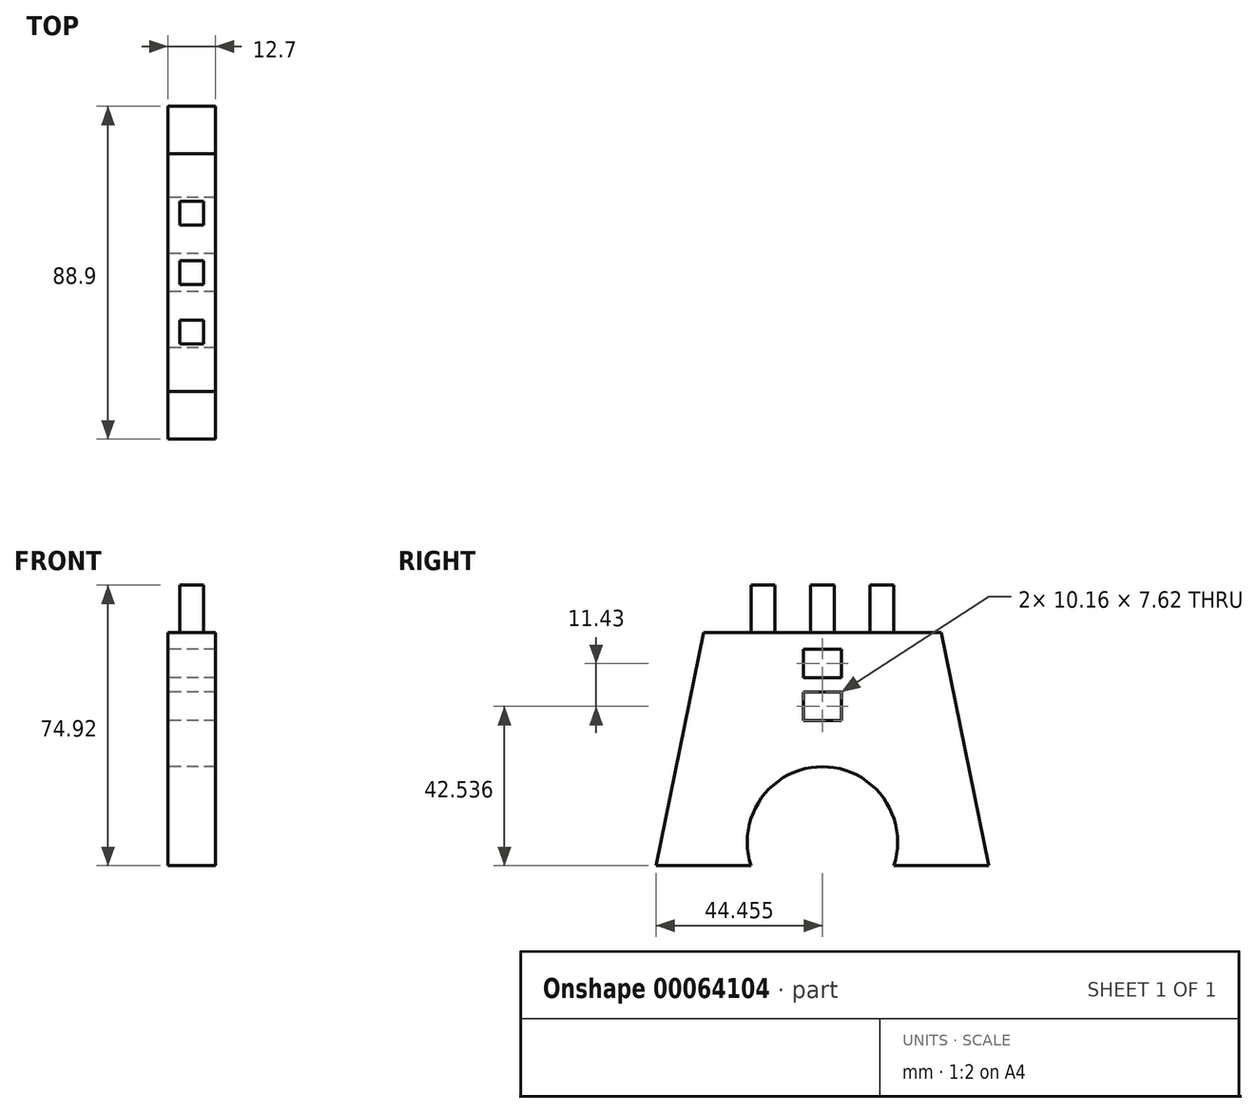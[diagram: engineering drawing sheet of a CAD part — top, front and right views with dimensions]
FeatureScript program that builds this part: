
annotation { "Feature Type Name" : "Feature", "Feature Type Description" : "" }
export const myFeature = defineFeature(function(context is Context, id is Id, definition is map)
    precondition{}
    {
        {
            var Q0;
            Q0=qCreatedBy(makeId("Right.planeOp"),FACE);
            var sketch = newSketch(context, id + "F0", { "sketchPlane" : qUnion([Q0])});
            skLineSegment(sketch, "E0", {"start": v(-34.03, -42.53) * mm, "end": v(-8.63, -42.53) * mm});
            skLineSegment(sketch, "E1", {"start": v(42.17, 19.7) * mm, "end": v(-21.33, 19.7) * mm});
            skLineSegment(sketch, "E2", {"start": v(-21.33, 19.7) * mm, "end": v(-34.03, -42.53) * mm});
            skLineSegment(sketch, "E3", {"start": v(42.17, 19.7) * mm, "end": v(54.87, -42.53) * mm});
            skArc(sketch, "E4", {"start": v(29.47, -42.53) * mm, "mid": v(10.42, -16.1) * mm, "end": v(-8.63, -42.53) * mm});
            skPoint(sketch, "E5.center.orphan", {"position": v(10.42, -42.53) * mm});
            skLineSegment(sketch, "E6.trimOffspring", {"start": v(29.47, -42.53) * mm, "end": v(54.87, -42.53) * mm});
            skLineSegment(sketch, "E7", {"start": v(10.42, 19.7) * mm, "end": v(10.42, 15.25) * mm, "construction": true});
            skLineSegment(sketch, "E8", {"start": v(10.42, -3.8) * mm, "end": v(15.5, -3.8) * mm});
            skLineSegment(sketch, "E9", {"start": v(15.5, -3.8) * mm, "end": v(15.5, 3.82) * mm});
            skLineSegment(sketch, "E10", {"start": v(15.5, 3.82) * mm, "end": v(10.42, 3.82) * mm});
            skLineSegment(sketch, "E11", {"start": v(10.42, 3.82) * mm, "end": v(10.42, 7.63) * mm});
            skLineSegment(sketch, "E12", {"start": v(10.42, 7.63) * mm, "end": v(15.5, 7.63) * mm});
            skLineSegment(sketch, "E13", {"start": v(15.5, 7.63) * mm, "end": v(15.5, 15.25) * mm});
            skLineSegment(sketch, "E14", {"start": v(15.5, 15.25) * mm, "end": v(10.42, 15.25) * mm});
            skLineSegment(sketch, "E15.MirrorCS", {"start": v(5.34, 3.82) * mm, "end": v(10.42, 3.82) * mm});
            skLineSegment(sketch, "E16.MirrorCS", {"start": v(5.34, -3.8) * mm, "end": v(5.34, 3.82) * mm});
            skLineSegment(sketch, "E17.MirrorCS", {"start": v(10.42, -3.8) * mm, "end": v(5.34, -3.8) * mm});
            skLineSegment(sketch, "E18.MirrorCS", {"start": v(10.42, 7.63) * mm, "end": v(5.34, 7.63) * mm});
            skLineSegment(sketch, "E19.MirrorCS", {"start": v(5.34, 7.63) * mm, "end": v(5.34, 15.25) * mm});
            skLineSegment(sketch, "E20.MirrorCS", {"start": v(5.34, 15.25) * mm, "end": v(10.42, 15.25) * mm});
            skLineSegment(sketch, "E21.trimOffspring", {"start": v(10.42, 7.63) * mm, "end": v(10.42, 3.82) * mm, "construction": true});
            skLineSegment(sketch, "E22.trimOffspring", {"start": v(10.42, -3.8) * mm, "end": v(10.42, -42.53) * mm, "construction": true});
            skSolve(sketch);
        }
        {
            var Q0;
            Q0 = qSketchRegion(id + "F0", true);
            extrude(context, id + "F1", {"entities" : qUnion([Q0]), "depth" : 12.7 * mm});
        }
        {
            var Q0;
            Q0=makeQuery(id+"F1.opExtrude","SWEPT_FACE",FACE,{"disambiguationData":[OSD([sQuery(id+"F0.wireOp",EDGE,"E1")])]});
            var sketch = newSketch(context, id + "F2", { "sketchPlane" : qUnion([Q0])});
            skLineSegment(sketch, "E23", {"start": v(6.35, 10.42) * mm, "end": v(12.7, 10.42) * mm, "construction": true});
            skPoint(sketch, "E24.orphan", {"position": v(0, 10.42) * mm});
            skLineSegment(sketch, "E25", {"start": v(9.53, 10.42) * mm, "end": v(9.53, 13.6) * mm});
            skLineSegment(sketch, "E26", {"start": v(0, 10.42) * mm, "end": v(6.35, 10.42) * mm, "construction": true});
            skLineSegment(sketch, "E27", {"start": v(3.18, 10.42) * mm, "end": v(3.18, 13.6) * mm});
            skLineSegment(sketch, "E28", {"start": v(3.17, 13.6) * mm, "end": v(9.52, 13.6) * mm});
            skLineSegment(sketch, "E29.MirrorCS", {"start": v(3.18, 10.42) * mm, "end": v(3.18, 7.25) * mm});
            skLineSegment(sketch, "E30.MirrorCS", {"start": v(9.53, 10.42) * mm, "end": v(9.53, 7.25) * mm});
            skLineSegment(sketch, "E31.MirrorCS", {"start": v(3.17, 7.25) * mm, "end": v(9.52, 7.25) * mm});
            skLineSegment(sketch, "E32", {"start": v(6.35, 10.42) * mm, "end": v(6.35, 42.17) * mm, "construction": true});
            skLineSegment(sketch, "E33", {"start": v(6.35, -21.33) * mm, "end": v(6.35, 10.42) * mm, "construction": true});
            skLineSegment(sketch, "E34", {"start": v(6.35, -5.45) * mm, "end": v(0, -5.45) * mm, "construction": true});
            skLineSegment(sketch, "E35", {"start": v(6.35, 26.3) * mm, "end": v(0, 26.3) * mm, "construction": true});
            skLineSegment(sketch, "E36", {"start": v(6.35, -5.45) * mm, "end": v(12.7, -5.45) * mm, "construction": true});
            skLineSegment(sketch, "E37", {"start": v(6.35, 26.3) * mm, "end": v(12.7, 26.3) * mm, "construction": true});
            skLineSegment(sketch, "E38", {"start": v(3.18, -5.45) * mm, "end": v(3.18, -2.28) * mm});
            skLineSegment(sketch, "E39", {"start": v(3.18, -2.28) * mm, "end": v(9.53, -2.28) * mm});
            skPoint(sketch, "E39.endSnap0", {"position": v(9.53, -5.45) * mm});
            skLineSegment(sketch, "E40", {"start": v(9.53, -2.28) * mm, "end": v(9.53, -5.45) * mm});
            skLineSegment(sketch, "E41", {"start": v(3.18, 26.3) * mm, "end": v(3.18, 29.47) * mm});
            skLineSegment(sketch, "E42", {"start": v(3.18, 29.47) * mm, "end": v(9.53, 29.47) * mm});
            skPoint(sketch, "E42.endSnap0", {"position": v(9.53, 26.3) * mm});
            skLineSegment(sketch, "E43", {"start": v(9.53, 29.47) * mm, "end": v(9.53, 26.3) * mm});
            skLineSegment(sketch, "E44.MirrorCS", {"start": v(3.18, -5.45) * mm, "end": v(3.18, -8.63) * mm});
            skLineSegment(sketch, "E45.MirrorCS", {"start": v(3.18, -8.63) * mm, "end": v(9.53, -8.63) * mm});
            skLineSegment(sketch, "E46.MirrorCS", {"start": v(9.53, -8.63) * mm, "end": v(9.53, -5.45) * mm});
            skLineSegment(sketch, "E47.MirrorCS", {"start": v(3.18, 26.3) * mm, "end": v(3.18, 23.12) * mm});
            skLineSegment(sketch, "E48.MirrorCS", {"start": v(3.18, 23.12) * mm, "end": v(9.53, 23.12) * mm});
            skLineSegment(sketch, "E49.MirrorCS", {"start": v(9.53, 23.12) * mm, "end": v(9.53, 26.3) * mm});
            skSolve(sketch);
        }
        {
            var Q0;
            Q0 = qSketchRegion(id + "F2", true);
            extrude(context, id + "F3", {"entities" : qUnion([Q0]), "operationType" : NewBodyOperationType.ADD, "depth" : 12.7 * mm});
        }
    });
